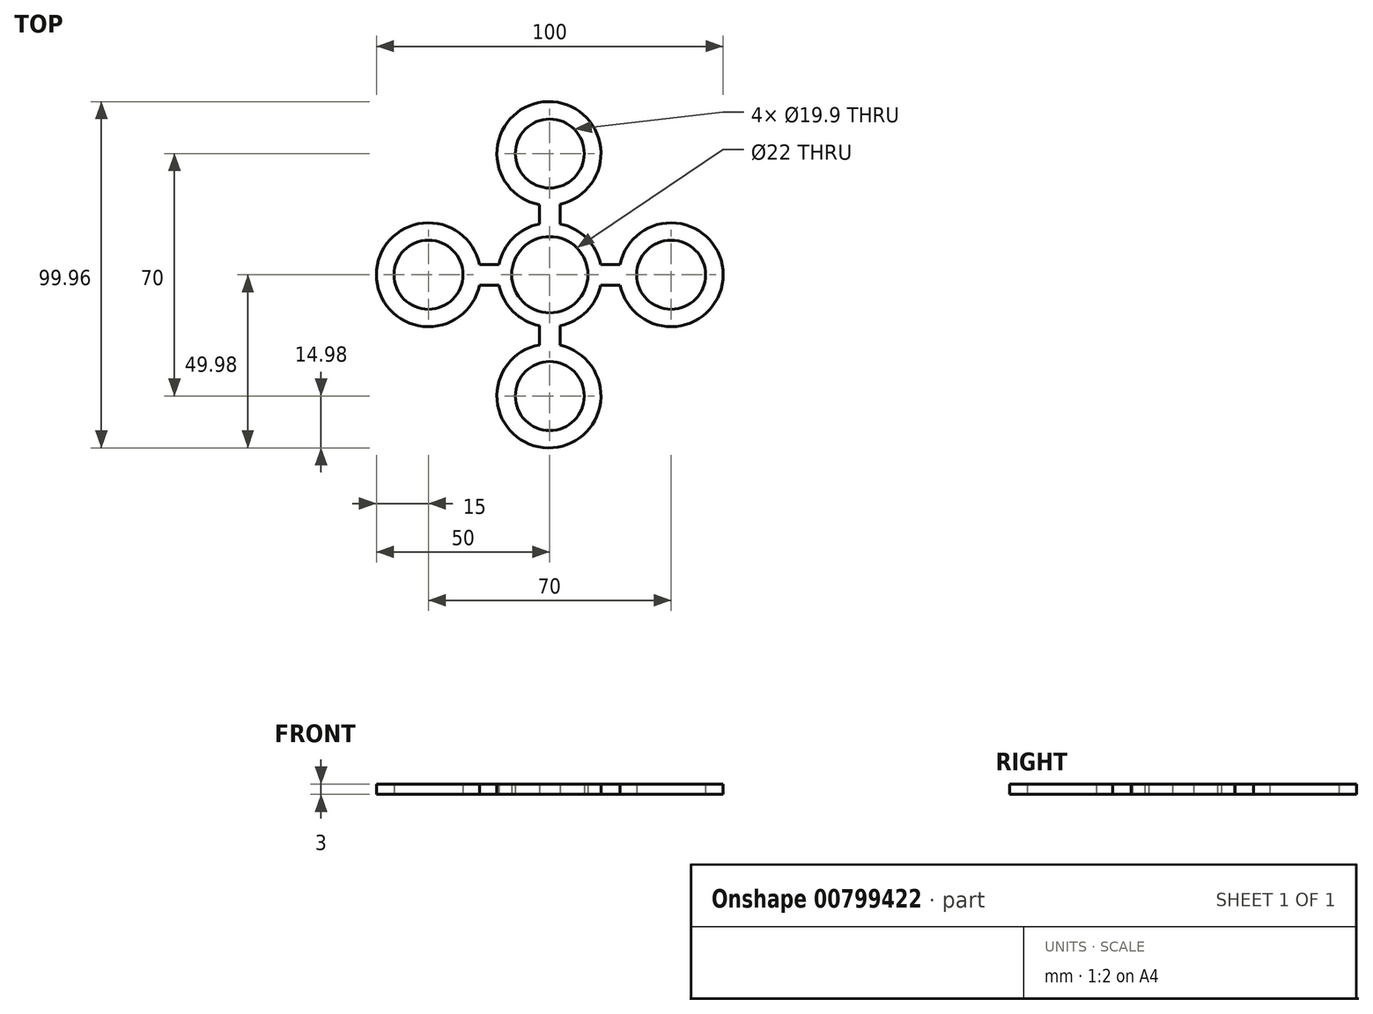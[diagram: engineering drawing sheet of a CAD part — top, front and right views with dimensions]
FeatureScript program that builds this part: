
annotation { "Feature Type Name" : "Feature", "Feature Type Description" : "" }
export const myFeature = defineFeature(function(context is Context, id is Id, definition is map)
    precondition{}
    {
        {
            var Q0;
            Q0=qCreatedBy(makeId("Top.planeOp"),FACE);
            var sketch = newSketch(context, id + "F0", { "sketchPlane" : qUnion([Q0])});
            skCircle(sketch, "E0", {"center": v(0, 0) * mm, "radius": 11 * mm});
            skLineSegment(sketch, "E1", {"start": v(-14.93, -1) * mm, "end": v(-14.93, -1) * mm});
            skArc(sketch, "E2.MirrorC", {"start": v(3, -20.34) * mm, "mid": v(-0.52, -49.98) * mm, "end": v(-3, -20.23) * mm});
            skCircle(sketch, "E3.MirrorC", {"center": v(0, -35) * mm, "radius": 9.95 * mm});
            skCircle(sketch, "E4.MirrorC", {"center": v(-35, 0) * mm, "radius": 9.95 * mm});
            skArc(sketch, "E5.MirrorC", {"start": v(-20.3, -3) * mm, "mid": v(-50, 0) * mm, "end": v(-20.3, 3) * mm});
            skArc(sketch, "E6.trimOffspring", {"start": v(3, -14.66) * mm, "mid": v(10.58, -10.58) * mm, "end": v(14.66, -3) * mm});
            skArc(sketch, "E7.MirrorCS", {"start": v(3, 20.34) * mm, "mid": v(-0.52, 49.98) * mm, "end": v(-3, 20.23) * mm});
            skCircle(sketch, "E8.MirrorC", {"center": v(0, 35) * mm, "radius": 9.95 * mm});
            skCircle(sketch, "E9.MirrorC", {"center": v(35, 0) * mm, "radius": 9.95 * mm});
            skArc(sketch, "E10.MirrorCS", {"start": v(20.3, -3) * mm, "mid": v(50, 0) * mm, "end": v(20.3, 3) * mm});
            skArc(sketch, "E11.trimOffspring", {"start": v(14.66, 3) * mm, "mid": v(10.58, 10.58) * mm, "end": v(3, 14.66) * mm});
            skArc(sketch, "E12.trimOffspring", {"start": v(-3, 14.66) * mm, "mid": v(-10.58, 10.58) * mm, "end": v(-14.66, 3) * mm});
            skLineSegment(sketch, "E13", {"start": v(-14.66, 3) * mm, "end": v(-20.3, 3) * mm});
            skLineSegment(sketch, "E14", {"start": v(-14.66, -3) * mm, "end": v(-20.3, -3) * mm});
            skArc(sketch, "E15.trimOffspring", {"start": v(-14.66, -3) * mm, "mid": v(-10.58, -10.58) * mm, "end": v(-3, -14.66) * mm});
            skLineSegment(sketch, "E16", {"start": v(-3, 14.66) * mm, "end": v(-3, 20.23) * mm});
            skLineSegment(sketch, "E17", {"start": v(3, 14.66) * mm, "end": v(3, 20.34) * mm});
            skLineSegment(sketch, "E18.MirrorCS", {"start": v(3, -14.66) * mm, "end": v(3, -20.34) * mm});
            skLineSegment(sketch, "E19.MirrorCS", {"start": v(-3, -14.66) * mm, "end": v(-3, -20.23) * mm});
            skLineSegment(sketch, "E20.MirrorCS", {"start": v(14.66, 3) * mm, "end": v(20.3, 3) * mm});
            skLineSegment(sketch, "E21.MirrorCS", {"start": v(14.66, -3) * mm, "end": v(20.3, -3) * mm});
            skSolve(sketch);
        }
        {
            var Q0;
            Q0=makeQuery(id+"F0.imprint","IMPRINT",FACE,{"disambiguationData":[TD([[makeQuery(id+"F0.imprint","IMPRINT",EDGE,{"derivedFrom":sQuery(id+"F0.wireOp",EDGE,"E0")}),-1.0]])]});
            extrude(context, id + "F1", {"entities" : qUnion([Q0]), "depth" : 3 * mm, "offsetDistance" : 25 * mm});
        }
    });
